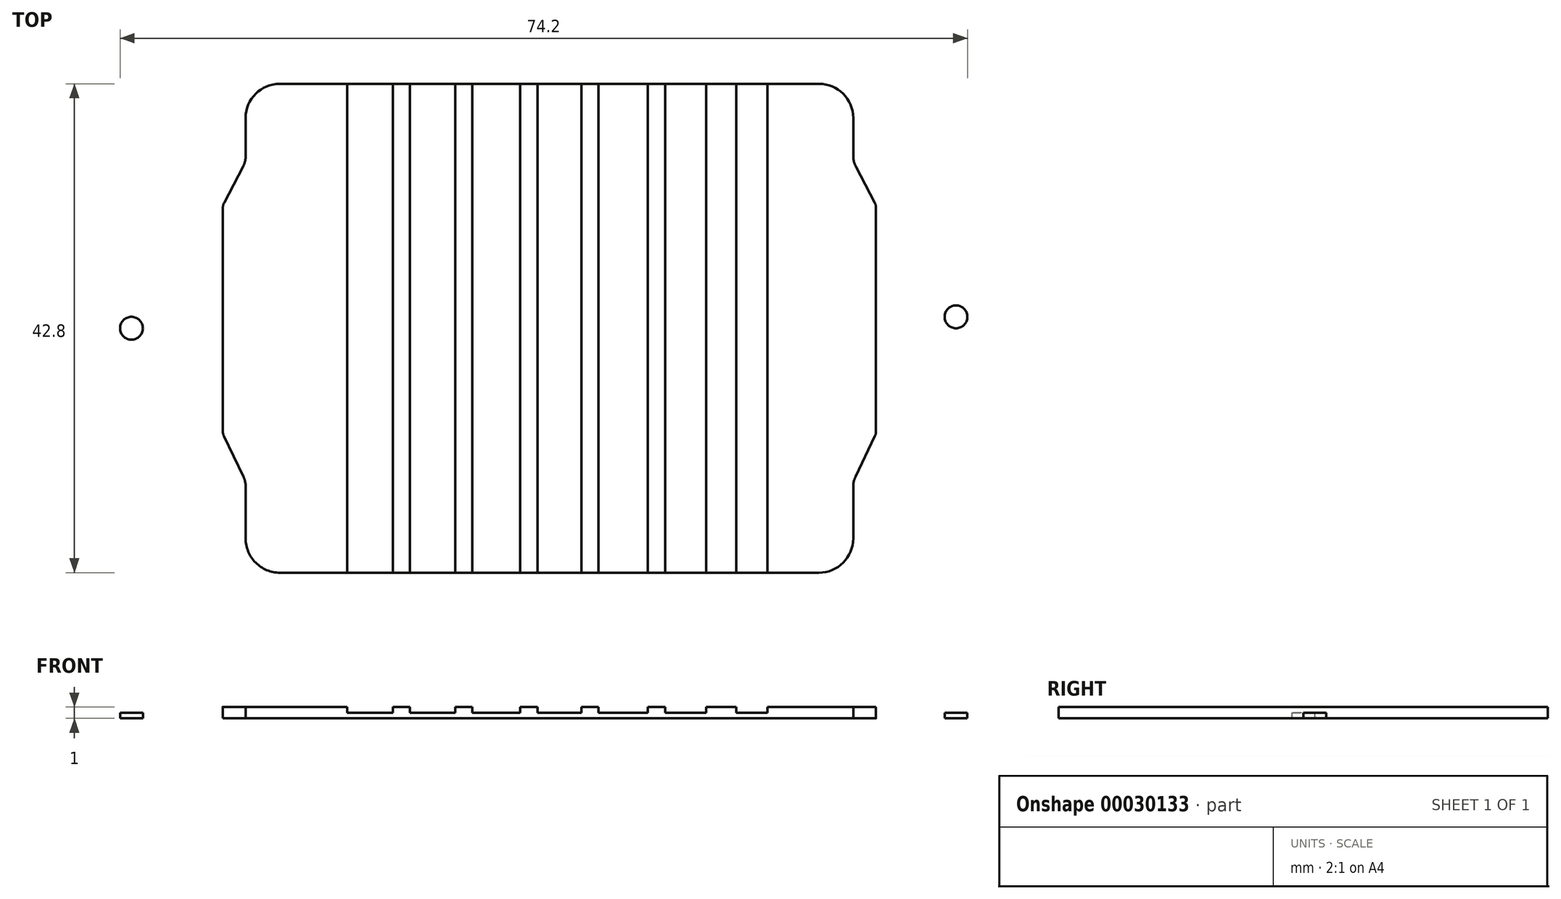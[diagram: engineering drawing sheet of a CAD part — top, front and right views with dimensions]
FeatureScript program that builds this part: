
annotation { "Feature Type Name" : "Feature", "Feature Type Description" : "" }
export const myFeature = defineFeature(function(context is Context, id is Id, definition is map)
    precondition{}
    {
        {
            var Q0;
            Q0=qCreatedBy(makeId("Top.planeOp"),FACE);
            var sketch = newSketch(context, id + "F0", { "sketchPlane" : qUnion([Q0])});
            skLineSegment(sketch, "E0", {"start": v(-26.6, -18.4) * mm, "end": v(-26.6, -13.86) * mm});
            skLineSegment(sketch, "E1", {"start": v(-26.6, -13.86) * mm, "end": v(-26.65, -13.41) * mm});
            skLineSegment(sketch, "E2", {"start": v(-26.65, -13.41) * mm, "end": v(-26.8, -13) * mm});
            skLineSegment(sketch, "E3", {"start": v(-26.8, -13) * mm, "end": v(-28.5, -9.44) * mm});
            skLineSegment(sketch, "E4", {"start": v(-28.5, -9.44) * mm, "end": v(-28.57, -9.23) * mm});
            skLineSegment(sketch, "E5", {"start": v(-28.57, -9.23) * mm, "end": v(-28.6, -9) * mm});
            skLineSegment(sketch, "E6", {"start": v(-28.6, -9) * mm, "end": v(-28.6, 10.52) * mm});
            skLineSegment(sketch, "E7", {"start": v(-28.6, 10.52) * mm, "end": v(-28.57, 10.76) * mm});
            skLineSegment(sketch, "E8", {"start": v(-28.57, 10.76) * mm, "end": v(-28.49, 10.99) * mm});
            skLineSegment(sketch, "E9", {"start": v(-28.49, 10.99) * mm, "end": v(-26.83, 14.16) * mm});
            skLineSegment(sketch, "E10", {"start": v(-26.83, 14.16) * mm, "end": v(-26.66, 14.61) * mm});
            skLineSegment(sketch, "E11", {"start": v(-26.66, 14.61) * mm, "end": v(-26.6, 15.09) * mm});
            skLineSegment(sketch, "E12", {"start": v(-26.6, 15.09) * mm, "end": v(-26.6, 18.4) * mm});
            skLineSegment(sketch, "E13", {"start": v(-26.6, 18.4) * mm, "end": v(-26.55, 18.95) * mm});
            skLineSegment(sketch, "E14", {"start": v(-26.55, 18.95) * mm, "end": v(-26.39, 19.5) * mm});
            skLineSegment(sketch, "E15", {"start": v(-26.39, 19.5) * mm, "end": v(-26.11, 20.04) * mm});
            skLineSegment(sketch, "E16", {"start": v(-26.11, 20.04) * mm, "end": v(-25.72, 20.52) * mm});
            skLineSegment(sketch, "E17", {"start": v(-25.72, 20.52) * mm, "end": v(-25.24, 20.91) * mm});
            skLineSegment(sketch, "E18", {"start": v(-25.24, 20.91) * mm, "end": v(-24.7, 21.2) * mm});
            skLineSegment(sketch, "E19", {"start": v(-24.7, 21.2) * mm, "end": v(-24.15, 21.35) * mm});
            skLineSegment(sketch, "E20", {"start": v(-24.15, 21.35) * mm, "end": v(-23.6, 21.4) * mm});
            skLineSegment(sketch, "E21", {"start": v(-23.6, 21.4) * mm, "end": v(23.6, 21.4) * mm});
            skLineSegment(sketch, "E22", {"start": v(23.6, 21.4) * mm, "end": v(24.15, 21.35) * mm});
            skLineSegment(sketch, "E23", {"start": v(24.15, 21.35) * mm, "end": v(24.7, 21.2) * mm});
            skLineSegment(sketch, "E24", {"start": v(24.7, 21.2) * mm, "end": v(25.24, 20.91) * mm});
            skLineSegment(sketch, "E25", {"start": v(25.24, 20.91) * mm, "end": v(25.72, 20.52) * mm});
            skLineSegment(sketch, "E26", {"start": v(25.72, 20.52) * mm, "end": v(26.11, 20.04) * mm});
            skLineSegment(sketch, "E27", {"start": v(26.11, 20.04) * mm, "end": v(26.39, 19.5) * mm});
            skLineSegment(sketch, "E28", {"start": v(26.39, 19.5) * mm, "end": v(26.55, 18.95) * mm});
            skLineSegment(sketch, "E29", {"start": v(26.55, 18.95) * mm, "end": v(26.6, 18.4) * mm});
            skLineSegment(sketch, "E30", {"start": v(26.6, 18.4) * mm, "end": v(26.6, 15.09) * mm});
            skLineSegment(sketch, "E31", {"start": v(26.6, 15.09) * mm, "end": v(26.66, 14.61) * mm});
            skLineSegment(sketch, "E32", {"start": v(26.66, 14.61) * mm, "end": v(26.83, 14.16) * mm});
            skLineSegment(sketch, "E33", {"start": v(26.83, 14.16) * mm, "end": v(28.49, 10.99) * mm});
            skLineSegment(sketch, "E34", {"start": v(28.49, 10.99) * mm, "end": v(28.57, 10.76) * mm});
            skLineSegment(sketch, "E35", {"start": v(28.57, 10.76) * mm, "end": v(28.6, 10.52) * mm});
            skLineSegment(sketch, "E36", {"start": v(28.6, 10.52) * mm, "end": v(28.6, -9) * mm});
            skLineSegment(sketch, "E37", {"start": v(28.6, -9) * mm, "end": v(28.57, -9.23) * mm});
            skLineSegment(sketch, "E38", {"start": v(28.57, -9.23) * mm, "end": v(28.5, -9.44) * mm});
            skLineSegment(sketch, "E39", {"start": v(28.5, -9.44) * mm, "end": v(26.8, -13) * mm});
            skLineSegment(sketch, "E40", {"start": v(26.8, -13) * mm, "end": v(26.65, -13.41) * mm});
            skLineSegment(sketch, "E41", {"start": v(26.65, -13.41) * mm, "end": v(26.6, -13.86) * mm});
            skLineSegment(sketch, "E42", {"start": v(26.6, -13.86) * mm, "end": v(26.6, -18.4) * mm});
            skLineSegment(sketch, "E43", {"start": v(26.6, -18.4) * mm, "end": v(26.55, -18.95) * mm});
            skLineSegment(sketch, "E44", {"start": v(26.55, -18.95) * mm, "end": v(26.39, -19.5) * mm});
            skLineSegment(sketch, "E45", {"start": v(26.39, -19.5) * mm, "end": v(26.11, -20.04) * mm});
            skLineSegment(sketch, "E46", {"start": v(26.11, -20.04) * mm, "end": v(25.72, -20.52) * mm});
            skLineSegment(sketch, "E47", {"start": v(25.72, -20.52) * mm, "end": v(25.24, -20.91) * mm});
            skLineSegment(sketch, "E48", {"start": v(25.24, -20.91) * mm, "end": v(24.7, -21.2) * mm});
            skLineSegment(sketch, "E49", {"start": v(24.7, -21.2) * mm, "end": v(24.15, -21.35) * mm});
            skLineSegment(sketch, "E50", {"start": v(24.15, -21.35) * mm, "end": v(23.6, -21.4) * mm});
            skLineSegment(sketch, "E51", {"start": v(23.6, -21.4) * mm, "end": v(-23.6, -21.4) * mm});
            skLineSegment(sketch, "E52", {"start": v(-23.6, -21.4) * mm, "end": v(-24.15, -21.35) * mm});
            skLineSegment(sketch, "E53", {"start": v(-24.15, -21.35) * mm, "end": v(-24.7, -21.2) * mm});
            skLineSegment(sketch, "E54", {"start": v(-24.7, -21.2) * mm, "end": v(-25.24, -20.91) * mm});
            skLineSegment(sketch, "E55", {"start": v(-25.24, -20.91) * mm, "end": v(-25.72, -20.52) * mm});
            skLineSegment(sketch, "E56", {"start": v(-25.72, -20.52) * mm, "end": v(-26.11, -20.04) * mm});
            skLineSegment(sketch, "E57", {"start": v(-26.11, -20.04) * mm, "end": v(-26.39, -19.5) * mm});
            skLineSegment(sketch, "E58", {"start": v(-26.39, -19.5) * mm, "end": v(-26.55, -18.95) * mm});
            skLineSegment(sketch, "E59", {"start": v(-26.55, -18.95) * mm, "end": v(-26.6, -18.4) * mm});
            skSolve(sketch);
        }
        {
            var Q0;
            Q0=qCreatedBy(makeId("Top.planeOp"),FACE);
            var sketch = newSketch(context, id + "F1", { "sketchPlane" : qUnion([Q0])});
            skLineSegment(sketch, "E60.0.0", {"start": v(-26.6, -13.86) * mm, "end": v(-26.6, -18.4) * mm});
            skLineSegment(sketch, "E60.0.9", {"start": v(-23.6, -21.4) * mm, "end": v(23.6, -21.4) * mm});
            skLineSegment(sketch, "E60.0.18", {"start": v(26.6, -18.4) * mm, "end": v(26.6, -13.86) * mm});
            skLineSegment(sketch, "E60.0.21", {"start": v(26.8, -13) * mm, "end": v(28.5, -9.44) * mm});
            skLineSegment(sketch, "E60.0.24", {"start": v(28.6, -9) * mm, "end": v(28.6, 10.52) * mm});
            skLineSegment(sketch, "E60.0.27", {"start": v(28.49, 10.99) * mm, "end": v(26.83, 14.16) * mm});
            skLineSegment(sketch, "E60.0.30", {"start": v(26.6, 15.09) * mm, "end": v(26.6, 18.4) * mm});
            skLineSegment(sketch, "E60.0.39", {"start": v(23.6, 21.4) * mm, "end": v(-23.6, 21.4) * mm});
            skLineSegment(sketch, "E60.0.48", {"start": v(-26.6, 18.4) * mm, "end": v(-26.6, 15.09) * mm});
            skLineSegment(sketch, "E60.0.51", {"start": v(-26.83, 14.16) * mm, "end": v(-28.49, 10.99) * mm});
            skLineSegment(sketch, "E60.0.54", {"start": v(-28.6, 10.52) * mm, "end": v(-28.6, -9) * mm});
            skLineSegment(sketch, "E60.0.57", {"start": v(-28.5, -9.44) * mm, "end": v(-26.8, -13) * mm});
            skArc(sketch, "E61", {"start": v(-23.6, 21.4) * mm, "mid": v(-25.72, 20.52) * mm, "end": v(-26.6, 18.4) * mm});
            skArc(sketch, "E62", {"start": v(-26.6, 15.09) * mm, "mid": v(-26.66, 14.61) * mm, "end": v(-26.83, 14.16) * mm});
            skArc(sketch, "E63", {"start": v(-28.49, 10.99) * mm, "mid": v(-28.57, 10.76) * mm, "end": v(-28.6, 10.52) * mm});
            skArc(sketch, "E64", {"start": v(-28.6, -9) * mm, "mid": v(-28.57, -9.23) * mm, "end": v(-28.5, -9.44) * mm});
            skArc(sketch, "E65", {"start": v(-26.8, -13) * mm, "mid": v(-26.65, -13.41) * mm, "end": v(-26.6, -13.86) * mm});
            skArc(sketch, "E66", {"start": v(-26.6, -18.4) * mm, "mid": v(-25.72, -20.52) * mm, "end": v(-23.6, -21.4) * mm});
            skArc(sketch, "E67", {"start": v(26.6, -18.4) * mm, "mid": v(25.72, -20.52) * mm, "end": v(23.6, -21.4) * mm});
            skArc(sketch, "E68", {"start": v(26.8, -13) * mm, "mid": v(26.65, -13.41) * mm, "end": v(26.6, -13.86) * mm});
            skArc(sketch, "E69", {"start": v(28.6, -9) * mm, "mid": v(28.57, -9.23) * mm, "end": v(28.5, -9.44) * mm});
            skArc(sketch, "E70", {"start": v(23.6, 21.4) * mm, "mid": v(25.72, 20.52) * mm, "end": v(26.6, 18.4) * mm});
            skArc(sketch, "E71", {"start": v(26.6, 15.09) * mm, "mid": v(26.66, 14.61) * mm, "end": v(26.83, 14.16) * mm});
            skArc(sketch, "E72", {"start": v(28.49, 10.99) * mm, "mid": v(28.57, 10.76) * mm, "end": v(28.6, 10.52) * mm});
            skSolve(sketch);
        }
        {
            var Q0;
            Q0=qCreatedBy(makeId("Top.planeOp"),FACE);
            var sketch = newSketch(context, id + "F2", { "sketchPlane" : qUnion([Q0])});
            skLineSegment(sketch, "E73", {"start": v(-17.1, 21.4) * mm, "end": v(-17.1, 4.36) * mm});
            skLineSegment(sketch, "E74", {"start": v(-12.35, 21.4) * mm, "end": v(-12.35, 4.36) * mm});
            skLineSegment(sketch, "E75", {"start": v(-10.85, 21.4) * mm, "end": v(-10.85, 4.36) * mm});
            skLineSegment(sketch, "E76", {"start": v(-6.92, 21.4) * mm, "end": v(-6.92, 4.36) * mm});
            skLineSegment(sketch, "E77", {"start": v(-5.42, 21.4) * mm, "end": v(-5.42, 4.36) * mm});
            skLineSegment(sketch, "E78", {"start": v(18.35, 21.4) * mm, "end": v(18.35, 4.36) * mm});
            skLineSegment(sketch, "E79", {"start": v(19.85, 21.4) * mm, "end": v(19.85, 4.36) * mm});
            skLineSegment(sketch, "E80", {"start": v(14.35, -21.4) * mm, "end": v(14.35, -6.23) * mm});
            skLineSegment(sketch, "E81", {"start": v(12.85, -21.4) * mm, "end": v(12.85, -6.78) * mm});
            skLineSegment(sketch, "E82", {"start": v(18.35, -21.4) * mm, "end": v(18.35, -7.05) * mm});
            skLineSegment(sketch, "E83", {"start": v(-1.5, 21.4) * mm, "end": v(-1.5, 4.36) * mm});
            skLineSegment(sketch, "E84", {"start": v(0, 21.4) * mm, "end": v(0, 4.36) * mm});
            skLineSegment(sketch, "E85", {"start": v(3.92, 21.4) * mm, "end": v(3.92, 4.36) * mm});
            skLineSegment(sketch, "E86", {"start": v(5.42, 21.4) * mm, "end": v(5.42, 4.36) * mm});
            skLineSegment(sketch, "E87", {"start": v(9.35, 21.4) * mm, "end": v(9.35, 4.36) * mm});
            skLineSegment(sketch, "E88", {"start": v(10.85, 21.4) * mm, "end": v(10.85, 4.36) * mm});
            skLineSegment(sketch, "E89", {"start": v(14.6, 21.4) * mm, "end": v(14.6, 4.36) * mm});
            skLineSegment(sketch, "E90", {"start": v(-17.1, 4.36) * mm, "end": v(-12.35, 4.36) * mm});
            skLineSegment(sketch, "E91.trimOffspring", {"start": v(-10.85, 4.36) * mm, "end": v(-6.92, 4.36) * mm});
            skLineSegment(sketch, "E92.trimOffspring", {"start": v(-5.42, 4.36) * mm, "end": v(-1.5, 4.36) * mm});
            skLineSegment(sketch, "E93.trimOffspring", {"start": v(0, 4.36) * mm, "end": v(3.92, 4.36) * mm});
            skLineSegment(sketch, "E94.trimOffspring", {"start": v(5.42, 4.36) * mm, "end": v(9.35, 4.36) * mm});
            skLineSegment(sketch, "E95.trimOffspring", {"start": v(10.85, 4.36) * mm, "end": v(14.6, 4.36) * mm});
            skLineSegment(sketch, "E96", {"start": v(14.6, 4.36) * mm, "end": v(18.35, 4.36) * mm});
            skLineSegment(sketch, "E97", {"start": v(9.4, -21.4) * mm, "end": v(9.4, -5.6) * mm});
            skLineSegment(sketch, "E98", {"start": v(7.9, -21.4) * mm, "end": v(7.9, -5.6) * mm});
            skLineSegment(sketch, "E99", {"start": v(3.15, -21.4) * mm, "end": v(3.15, -4.7) * mm});
            skLineSegment(sketch, "E100", {"start": v(-3.6, -21.4) * mm, "end": v(-3.6, -3.8) * mm});
            skLineSegment(sketch, "E101", {"start": v(-2.1, -21.4) * mm, "end": v(-2.1, -3.53) * mm});
            skLineSegment(sketch, "E102", {"start": v(-8.1, -2.9) * mm, "end": v(-8.1, -21.4) * mm});
            skLineSegment(sketch, "E103", {"start": v(-9.6, -2.71) * mm, "end": v(-9.6, -21.4) * mm});
            skLineSegment(sketch, "E104", {"start": v(-13.6, -2.44) * mm, "end": v(-13.6, -21.4) * mm});
            skLineSegment(sketch, "E105", {"start": v(-15.1, -1.63) * mm, "end": v(-15.1, -21.4) * mm});
            skLineSegment(sketch, "E106", {"start": v(1.65, -4.7) * mm, "end": v(1.65, -21.4) * mm});
            skLineSegment(sketch, "E107", {"start": v(-18.35, -0.55) * mm, "end": v(-18.35, -21.4) * mm});
            skSolve(sketch);
        }
        {
            var Q0;
            Q0=qCreatedBy(makeId("Top.planeOp"),FACE);
            var sketch = newSketch(context, id + "F3", { "sketchPlane" : qUnion([Q0])});
            skLineSegment(sketch, "E108", {"start": v(-18.35, 1.13) * mm, "end": v(-17.1, 1.13) * mm});
            skPoint(sketch, "E109", {"position": v(-17.72, 1.13) * mm});
            skLineSegment(sketch, "E110", {"start": v(-17.72, 21.4) * mm, "end": v(-17.72, -21.4) * mm});
            skLineSegment(sketch, "E111", {"start": v(18.35, -2.1) * mm, "end": v(19.85, -2.1) * mm});
            skPoint(sketch, "E112", {"position": v(19.1, -2.1) * mm});
            skLineSegment(sketch, "E113", {"start": v(19.1, 21.4) * mm, "end": v(19.1, -21.4) * mm});
            skLineSegment(sketch, "E114", {"start": v(-15.1, 7.79) * mm, "end": v(-12.35, 7.79) * mm});
            skPoint(sketch, "E115", {"position": v(-13.72, 7.79) * mm});
            skLineSegment(sketch, "E116", {"start": v(-13.72, 23.74) * mm, "end": v(-13.72, -24.91) * mm});
            skLineSegment(sketch, "E117", {"start": v(-10.85, 0.76) * mm, "end": v(-13.6, 0.76) * mm});
            skLineSegment(sketch, "E118", {"start": v(-12.22, 23.8) * mm, "end": v(-12.22, -24.9) * mm});
            skPoint(sketch, "E119", {"position": v(-12.22, 0.76) * mm});
            skLineSegment(sketch, "E120", {"start": v(-9.6, -8.2) * mm, "end": v(-6.92, -8.2) * mm});
            skPoint(sketch, "E121", {"position": v(-8.26, -8.2) * mm});
            skLineSegment(sketch, "E122", {"start": v(-8.26, 23.8) * mm, "end": v(-8.26, -29.82) * mm});
            skLineSegment(sketch, "E123", {"start": v(-8.1, -0.99) * mm, "end": v(-5.42, -0.99) * mm});
            skPoint(sketch, "E124", {"position": v(-6.76, -0.99) * mm});
            skLineSegment(sketch, "E125", {"start": v(-6.76, 24.6) * mm, "end": v(-6.76, -33.08) * mm});
            skLineSegment(sketch, "E126", {"start": v(-3.6, 2.8) * mm, "end": v(-1.5, 2.8) * mm});
            skLineSegment(sketch, "E127", {"start": v(-2.1, -1.2) * mm, "end": v(0, -1.2) * mm});
            skPoint(sketch, "E128", {"position": v(-2.55, 2.8) * mm});
            skPoint(sketch, "E129", {"position": v(-1.05, -1.2) * mm});
            skLineSegment(sketch, "E130", {"start": v(-2.55, 22.97) * mm, "end": v(-2.55, -30.62) * mm});
            skLineSegment(sketch, "E131", {"start": v(-1.05, 22.97) * mm, "end": v(-1.05, -30.86) * mm});
            skLineSegment(sketch, "E132", {"start": v(1.65, -3.07) * mm, "end": v(3.92, -3.07) * mm});
            skLineSegment(sketch, "E133", {"start": v(3.15, 1.97) * mm, "end": v(5.42, 1.97) * mm});
            skPoint(sketch, "E134", {"position": v(2.79, -3.07) * mm});
            skPoint(sketch, "E135", {"position": v(4.29, 1.97) * mm});
            skLineSegment(sketch, "E136", {"start": v(2.79, 25.71) * mm, "end": v(2.79, -35.53) * mm});
            skLineSegment(sketch, "E137", {"start": v(4.29, 25.2) * mm, "end": v(4.29, -33.59) * mm});
            skLineSegment(sketch, "E138", {"start": v(7.9, 2.8) * mm, "end": v(9.35, 2.8) * mm});
            skLineSegment(sketch, "E139", {"start": v(9.4, -7.12) * mm, "end": v(10.85, -7.12) * mm});
            skPoint(sketch, "E140", {"position": v(8.62, 2.8) * mm});
            skPoint(sketch, "E141", {"position": v(10.12, -7.12) * mm});
            skLineSegment(sketch, "E142", {"start": v(8.62, 23.87) * mm, "end": v(8.62, -29.7) * mm});
            skLineSegment(sketch, "E143", {"start": v(10.12, 23.3) * mm, "end": v(10.12, -28.43) * mm});
            skLineSegment(sketch, "E144", {"start": v(14.35, -3.57) * mm, "end": v(18.35, -3.57) * mm});
            skLineSegment(sketch, "E145", {"start": v(12.85, -9.15) * mm, "end": v(14.6, -9.15) * mm});
            skPoint(sketch, "E146", {"position": v(13.72, -9.15) * mm});
            skPoint(sketch, "E147", {"position": v(16.35, -3.57) * mm});
            skLineSegment(sketch, "E148", {"start": v(13.72, 23.45) * mm, "end": v(13.72, -28.87) * mm});
            skLineSegment(sketch, "E149", {"start": v(16.35, 24.26) * mm, "end": v(16.35, -29.92) * mm});
            skSolve(sketch);
        }
        {
            var Q0;
            Q0=qCreatedBy(makeId("Top.planeOp"),FACE);
            var sketch = newSketch(context, id + "F4", { "sketchPlane" : qUnion([Q0])});
            skLineSegment(sketch, "E150.0", {"start": v(-26.6, -13.86) * mm, "end": v(-26.6, -18.4) * mm});
            skLineSegment(sketch, "E150.1", {"start": v(-23.6, -21.4) * mm, "end": v(23.6, -21.4) * mm});
            skLineSegment(sketch, "E150.2", {"start": v(26.6, -18.4) * mm, "end": v(26.6, -13.86) * mm});
            skLineSegment(sketch, "E150.3", {"start": v(26.8, -13) * mm, "end": v(28.5, -9.44) * mm});
            skLineSegment(sketch, "E150.4", {"start": v(28.6, -9) * mm, "end": v(28.6, 10.52) * mm});
            skLineSegment(sketch, "E150.5", {"start": v(28.49, 10.99) * mm, "end": v(26.83, 14.16) * mm});
            skLineSegment(sketch, "E150.6", {"start": v(26.6, 15.09) * mm, "end": v(26.6, 18.4) * mm});
            skLineSegment(sketch, "E150.7", {"start": v(23.6, 21.4) * mm, "end": v(-23.6, 21.4) * mm});
            skLineSegment(sketch, "E150.8", {"start": v(-26.6, 18.4) * mm, "end": v(-26.6, 15.09) * mm});
            skLineSegment(sketch, "E150.9", {"start": v(-26.83, 14.16) * mm, "end": v(-28.49, 10.99) * mm});
            skLineSegment(sketch, "E150.10", {"start": v(-28.6, 10.52) * mm, "end": v(-28.6, -9) * mm});
            skLineSegment(sketch, "E150.11", {"start": v(-28.5, -9.44) * mm, "end": v(-26.8, -13) * mm});
            skArc(sketch, "E150.12", {"start": v(-23.6, 21.4) * mm, "mid": v(-25.72, 20.52) * mm, "end": v(-26.6, 18.4) * mm});
            skArc(sketch, "E150.13", {"start": v(-26.6, 15.09) * mm, "mid": v(-26.66, 14.61) * mm, "end": v(-26.83, 14.16) * mm});
            skArc(sketch, "E150.14", {"start": v(-28.49, 10.99) * mm, "mid": v(-28.57, 10.76) * mm, "end": v(-28.6, 10.52) * mm});
            skArc(sketch, "E150.15", {"start": v(-28.6, -9) * mm, "mid": v(-28.57, -9.23) * mm, "end": v(-28.5, -9.44) * mm});
            skArc(sketch, "E150.16", {"start": v(-26.8, -13) * mm, "mid": v(-26.65, -13.41) * mm, "end": v(-26.6, -13.86) * mm});
            skArc(sketch, "E150.17", {"start": v(-26.6, -18.4) * mm, "mid": v(-25.72, -20.52) * mm, "end": v(-23.6, -21.4) * mm});
            skArc(sketch, "E150.18", {"start": v(26.6, -18.4) * mm, "mid": v(25.72, -20.52) * mm, "end": v(23.6, -21.4) * mm});
            skArc(sketch, "E150.19", {"start": v(26.8, -13) * mm, "mid": v(26.65, -13.41) * mm, "end": v(26.6, -13.86) * mm});
            skArc(sketch, "E150.20", {"start": v(28.6, -9) * mm, "mid": v(28.57, -9.23) * mm, "end": v(28.5, -9.44) * mm});
            skArc(sketch, "E150.21", {"start": v(23.6, 21.4) * mm, "mid": v(25.72, 20.52) * mm, "end": v(26.6, 18.4) * mm});
            skArc(sketch, "E150.22", {"start": v(26.6, 15.09) * mm, "mid": v(26.66, 14.61) * mm, "end": v(26.83, 14.16) * mm});
            skArc(sketch, "E150.23", {"start": v(28.49, 10.99) * mm, "mid": v(28.57, 10.76) * mm, "end": v(28.6, 10.52) * mm});
            skLineSegment(sketch, "E151.0", {"start": v(19.1, 21.4) * mm, "end": v(19.1, -21.4) * mm});
            skLineSegment(sketch, "E151.1", {"start": v(16.35, 21.4) * mm, "end": v(16.35, -21.4) * mm});
            skLineSegment(sketch, "E151.2", {"start": v(13.72, 21.4) * mm, "end": v(13.72, -21.4) * mm});
            skLineSegment(sketch, "E151.3", {"start": v(10.12, 21.4) * mm, "end": v(10.12, -21.4) * mm});
            skLineSegment(sketch, "E151.4", {"start": v(8.62, 21.4) * mm, "end": v(8.62, -21.4) * mm});
            skLineSegment(sketch, "E151.5", {"start": v(4.29, 21.4) * mm, "end": v(4.29, -21.4) * mm});
            skLineSegment(sketch, "E151.6", {"start": v(2.79, 21.4) * mm, "end": v(2.79, -21.4) * mm});
            skLineSegment(sketch, "E151.7", {"start": v(-1.05, 21.4) * mm, "end": v(-1.05, -21.4) * mm});
            skLineSegment(sketch, "E151.8", {"start": v(-2.55, 21.4) * mm, "end": v(-2.55, -21.4) * mm});
            skLineSegment(sketch, "E151.9", {"start": v(-6.76, 21.4) * mm, "end": v(-6.76, -21.4) * mm});
            skLineSegment(sketch, "E151.10", {"start": v(-8.26, 21.4) * mm, "end": v(-8.26, -21.4) * mm});
            skLineSegment(sketch, "E151.11", {"start": v(-12.22, 21.4) * mm, "end": v(-12.22, -21.4) * mm});
            skLineSegment(sketch, "E151.12", {"start": v(-13.72, 21.4) * mm, "end": v(-13.72, -21.4) * mm});
            skLineSegment(sketch, "E151.13", {"start": v(-17.72, 21.4) * mm, "end": v(-17.72, -21.4) * mm});
            skSolve(sketch);
        }
        {
            var Q0;
            Q0=makeQuery(id+"F4.imprint","IMPRINT",FACE,{"disambiguationData":[TD([[makeQuery(id+"F4.imprint","IMPRINT",EDGE,{"derivedFrom":sQuery(id+"F4.wireOp",EDGE,"E150.0")}),1.0]])]});
            extrude(context, id + "F5", {"entities" : qUnion([Q0]), "depth" : 1 * mm});
        }
        {
            var Q0;
            {var subQ1=sQuery(id+"F4.wireOp",EDGE,"E151.11");Q0=makeQuery(id+"F4.imprint","IMPRINT",FACE,{"disambiguationData":[TD([[makeQuery(id+"F4.imprint","IMPRINT",EDGE,{"derivedFrom":subQ1}),-1.0]])]});}
            extrude(context, id + "F6", {"entities" : qUnion([Q0]), "depth" : 1 * mm});
        }
        {
            var Q0;
            {var subQ1=sQuery(id+"F4.wireOp",EDGE,"E151.9");Q0=makeQuery(id+"F4.imprint","IMPRINT",FACE,{"disambiguationData":[TD([[makeQuery(id+"F4.imprint","IMPRINT",EDGE,{"derivedFrom":subQ1}),-1.0]])]});}
            extrude(context, id + "F7", {"entities" : qUnion([Q0]), "depth" : 1 * mm});
        }
        {
            var Q0;
            {var subQ1=sQuery(id+"F4.wireOp",EDGE,"E151.7");Q0=makeQuery(id+"F4.imprint","IMPRINT",FACE,{"disambiguationData":[TD([[makeQuery(id+"F4.imprint","IMPRINT",EDGE,{"derivedFrom":subQ1}),-1.0]])]});}
            extrude(context, id + "F8", {"entities" : qUnion([Q0]), "depth" : 1 * mm});
        }
        {
            var Q0;
            {var subQ1=sQuery(id+"F4.wireOp",EDGE,"E151.5");Q0=makeQuery(id+"F4.imprint","IMPRINT",FACE,{"disambiguationData":[TD([[makeQuery(id+"F4.imprint","IMPRINT",EDGE,{"derivedFrom":subQ1}),-1.0]])]});}
            extrude(context, id + "F9", {"entities" : qUnion([Q0]), "depth" : 1 * mm});
        }
        {
            var Q0;
            {var subQ1=sQuery(id+"F4.wireOp",EDGE,"E151.3");Q0=makeQuery(id+"F4.imprint","IMPRINT",FACE,{"disambiguationData":[TD([[makeQuery(id+"F4.imprint","IMPRINT",EDGE,{"derivedFrom":subQ1}),-1.0]])]});}
            extrude(context, id + "F10", {"entities" : qUnion([Q0]), "depth" : 1 * mm});
        }
        {
            var Q0;
            {var subQ1=sQuery(id+"F4.wireOp",EDGE,"E151.1");Q0=makeQuery(id+"F4.imprint","IMPRINT",FACE,{"disambiguationData":[TD([[makeQuery(id+"F4.imprint","IMPRINT",EDGE,{"derivedFrom":subQ1}),-1.0]])]});}
            extrude(context, id + "F11", {"entities" : qUnion([Q0]), "depth" : 1 * mm});
        }
        {
            var Q0;
            Q0=makeQuery(id+"F4.imprint","IMPRINT",FACE,{"disambiguationData":[TD([[makeQuery(id+"F4.imprint","IMPRINT",EDGE,{"derivedFrom":sQuery(id+"F4.wireOp",EDGE,"E150.2")}),1.0]])]});
            extrude(context, id + "F12", {"entities" : qUnion([Q0]), "depth" : 1 * mm});
        }
        {
            var Q0;
            Q0 = qSketchRegion(id + "F1", true);
            extrude(context, id + "F13", {"entities" : qUnion([Q0]), "operationType" : NewBodyOperationType.ADD, "depth" : 0.5 * mm});
        }
        {
            var Q0;
            Q0=qCreatedBy(makeId("Top.planeOp"),FACE);
            var sketch = newSketch(context, id + "F14", { "sketchPlane" : qUnion([Q0])});
            skCircle(sketch, "E152", {"center": v(-36.6, 0) * mm, "radius": 1 * mm});
            skCircle(sketch, "E153", {"center": v(35.6, 1) * mm, "radius": 1 * mm});
            skSolve(sketch);
        }
        {
            var Q0;
            Q0 = qSketchRegion(id + "F14", true);
            extrude(context, id + "F15", {"entities" : qUnion([Q0]), "depth" : 0.5 * mm});
        }
    });
